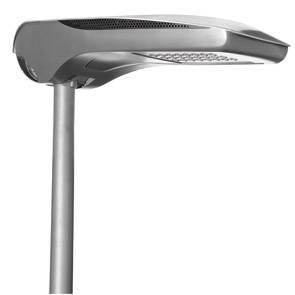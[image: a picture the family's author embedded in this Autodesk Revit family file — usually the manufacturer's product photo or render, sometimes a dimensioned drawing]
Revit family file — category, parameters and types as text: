
# Revit family: Lighting-StreetLighting-GEWISS-STREET[O3]-LED_OPTIC_ST1
name_source: partatom
category: Apparecchi per illuminazione
units: mm (PartAtom-declared; Revit-internal decimal feet)

## family parameters
Basato su piano di lavoro = No
Condiviso = No
Numero OmniClass = 23.80.70.14.21
Punto di calcolo locali = No
Quota connettore circolare = Usa diametro
Sempre verticale = Sì
Sorgente d'illuminazione = No
Taglio con vuoti quando caricato = No
Tipo di parte = Normale
Titolo OmniClass = Street and Roadway Lighting

## types (15) — shared parameters
Altezza da terra testa staffa = 822 mm
Application = External
Carico apparente = 68 VA
Catalogue = LIGHTING
Catalogue Range = STREET [O3]
Colour = Graphite/Aluminium
Commenti sul wattaggio = 68W
IDF = e1037118-10e4-4194-a64e-daf49fc1f628
IDT = a85e433dc89b4111a164f9b8ba35bb1e
IP degree = IP66
Immagine tipo = GW87502.jpg
Insulation class = II
LED Life time (L80B10) = 100000H
LED Life time (L90B20) = 50000H
L_staffa = 120 mm  [stored 0.393701 ft]
Lamp = LED
Lampada = LED
Maximum surface exposed to the wind = 0,26M2
Minimum distance from the illuminated object = 1M
Numero di poli = 2
Optic = ST1 - ULOR: 0%
Photobiologic Risk = RG1/RG2 @ 20cm
Produttore = GEWISS S.p.A.
SEO = Street lighting
Shock resistance = IK08 BODY - IK06 LENS
Struttura = <Per categoria>
Technical sheet = https://www.gewiss.com
Tilt adjustable = ±20° bracket - 0°÷20° pole head
URL = https://www.gewiss.com
Version file RFA = 20.11
Vetro = GEWISS - Led - lm 650 / Temp_3000_K
Voltage: = 220/240 V - 50/60 Hz
Voltaggio = 230 V
Warranty = 5 years

## per-type parameters (varying)
| type | Colour temperature | Colour temperature: | Descrizione | Driver type | EAN code | Electrocod | LED LifeTime (L80B20) | LED current | Lumen output (lm) | Material | Modello | No. Chorus modules | Nominal flux (lm) | Number of modules | Operating temperature: | Power supply operation | Risk photobiological | System power | Typology | Voltage | Weight (kg) | Weight (kg): | Working temperature |
| GW87413 - STREET LED 4M 4000K 700mA STR. | 4000 K (CRI 70) | 4000 K (CRI 70) | STREET LED 4M 4000K 700mA STR. | Constant Current Driver Led | 8011564830615 | 244C | 50000H | 700 mA | 12900 | Die-cast  aluminium | GW87413 | 4 (4x16 LED) | 15370 | 4 (4x16 LED) | -25 +35 °C |  | RG1/RG2 @ 20cm | 131W | Stand alone | 220/240 V - 50/60 Hz - Stand alone and/or possibility of dimmer 1-10 V | 10,3 | 10,3 | -25 +25 °C |
| GW87531 - STREET LED BIREG.2M 4000K 550mA STR | 4000 K (CRI 70) | 4000 K (CRI 70) | STREET LED BI-PO. 2M 4000K 530mA STREET | Constant Current Driver Led | 8011564782914 | 244C | 50000H | 530mA | 5890 | Die-cast  aluminium | GW87531 | 2 (2x16 LED) | 7020 | 2 (2x16 LED) | -25 +50 °C | Bi power | RG1/RG2 @ 20cm | 54W |  | 220/240 V - 50/60 Hz - Bi-power with self-learning | 9,1 | 9,1 | -25 +25 °C |
| GW87412V - STREET LED 3M 4000K 700mA STREET |  | 4000 K (CRI>70) | STREET LED 3M 4000K 700mA STR |  |  | 244C |  | 700 mA | 9860 |  | GW87412V |  | 11740 | 3 (3x16 LED) | -25 +25 °C |  |  | 99W | Programmable (5 step) | 220/240 V - 50/60 Hz - Stand alone e/o Programmabile 5 Step |  | 9,59999999999999 |  |
| GW87534 - STREET LED BIREG.5M 4000K 550mA STR | 4000 K (CRI 70) | 4000 K (CRI 70) | STREET LED BI-PO. 5M 4000K 530mA STREET | Constant Current Driver Led | 8011564782945 | 244B | 50000H | 530mA | 13870 | Die-cast  aluminium | GW87534 | 5 (5x16 LED) | 16530 | 5 (5x16 LED) | -25 +40 °C | Bi power | RG1/RG2 @ 20cm | 129W |  | 220/240 V - 50/60 Hz - Bi-power with self-learning | 10,9 | 10,9 | -25 +25 °C |
| GW87413V - STREET LED 4M 4000K 700mA STR. |  | 4000 K (CRI>70) | STREET LED 4M 4000K 700mA STR |  |  | 244C |  | 700 mA | 12900 |  | GW87413V |  | 15370 | 4 (4x16 LED) | -25 +25 °C |  |  | 131W | Programmable (5 step) | 220/240 V - 50/60 Hz - Stand alone e/o Programmabile 5 Step |  | 10,3 |  |
| GW87410 - STREET LED 1M 4000K 700mA STREET | 4000 K (CRI 70) | 4000 K (CRI 70) | STREET LED 1M 4000K 700mA STREET | Constant Current Driver Led | 8011564804654 | 244C | 50000H | 700 mA | 3470 | Die-cast  aluminium | GW87410 | 1 (1x16 LED) | 4140 | 1 (1x16 LED) | -25 +50 °C |  | RG1/RG2 @ 20cm | 37W | Stand alone | 220/240 V - 50/60 Hz - Stand alone and/or possibility of dimmer 1-10 V | 8,5 | 8,5 | -25 +25 °C |
| GW87414 - STREET ST1 5M 4000K 550mA 220/240 | 4000 K (CRI 70) | 4000 K (CRI 70) | STREET ST1 5M 4000K 550mA 220/240 | Constant Current Driver Led | 8011564863125 | 244C | 50000H | 550 mA | 13740 | Die-cast  aluminium | GW87414 | 5 (5x16 LED) | 16360 | 5 (5x16 LED) | -25 +40 °C |  | RG1/RG2 @ 20cm | 127W | Stand alone | 220/240 V - 50/60 Hz - Stand alone and/or possibility of dimmer 1-10 V | 10,9 | 10,9 | -25 +25 °C |
| GW87414V - STREET ST1 5M 4000K 550mA 220/240 |  | 4000 K (CRI>70) | STREET ST1 5M 4000K 550mA 220/240 |  |  | 244C |  | 550 mA | 13740 |  | GW87414V |  | 16360 | 5 (5x16 LED) | -25 +25 °C |  |  | 127W | Programmable (5 step) | 220/240 V - 50/60 Hz - Stand alone e/o Programmabile 5 Step |  | 10,9 |  |
| GW87410V - STREET LED 1M 4000K 700mA STREET |  | 4000 K (CRI>70) | STREET LED 1M 4000K 700mA STR |  |  | 244C |  | 700 mA | 3470 |  | GW87410V |  | 4140 | 1 (1x16 LED) | -25 +25 °C |  |  | 37W | Programmable (5 step) | 220/240 V - 50/60 Hz - Stand alone e/o Programmabile 5 Step |  | 8,5 |  |
| GW87412 - STREET LED 3M 4000K 700mA STREET | 4000 K (CRI 70) | 4000 K (CRI 70) | STREET LED 3M 4000K 700mA STREET | Constant Current Driver Led | 8011564804630 | 244C | 50000H | 700 mA | 9860 | Die-cast  aluminium | GW87412 | 3 (3x16 LED) | 11740 | 3 (3x16 LED) | -25 +40 °C |  | RG1/RG2 @ 20cm | 99W | Stand alone | 220/240 V - 50/60 Hz - Stand alone and/or possibility of dimmer 1-10 V | 9,6 | 9,6 | -25 +25 °C |
| GW87411V - STREET LED 2M 4000K 700mA STREET |  | 4000 K (CRI>70) | STREET LED 2M 4000K 700mA STR |  |  | 244C |  | 700 mA | 6760 |  | GW87411V |  | 8050 | 2 (2x16 LED) | -25 +25 °C |  |  | 68W | Programmable (5 step) | 220/240 V - 50/60 Hz - Stand alone e/o Programmabile 5 Step |  | 9,09999999999999 |  |
| GW87530 - STREET LED BIREG.1M 4000K 550mA STR | 4000 K (CRI 70) | 4000 K (CRI 70) | STREET LED BI-PO. 1M 4000K 530mA STREET | Constant Current Driver Led | 8011564804661 | 244C | 50000H | 530mA | 3030 | Die-cast  aluminium | GW87530 | 1 (1x16 LED) | 3610 | 1 (1x16 LED) | -25 +50 °C | Bi power | RG1/RG2 @ 20cm | 31W |  | 220/240 V - 50/60 Hz - Bi-power with self-learning | 8,5 | 8,5 | -25 +25 °C |
| GW87533 - STREET LED BIREG.4M 4000K 550mA STR | 4000 K (CRI 70) | 4000 K (CRI 70) | STREET LED BI-PO. 4M 4000K 530mA STREET | Constant Current Driver Led | 8011564782938 | 244C | 50000H | 530mA | 11240 | Die-cast  aluminium | GW87533 | 4 (4x16 LED) | 13400 | 4 (4x16 LED) | -25 +50 °C | Bi power | RG1/RG2 @ 20cm | 105W |  | 220/240 V - 50/60 Hz - Bi-power with self-learning | 10,3 | 10,3 | -25 +25 °C |
| GW87411 - STREET LED 2M 4000K 700mA STREET | 4000 K (CRI 70) | 4000 K (CRI 70) | STREET LED 2M 4000K 700mA STREET | Constant Current Driver Led | 8011564804647 | 244C | 50000H | 700 mA | 6760 | Die-cast  aluminium | GW87411 | 2 (2x16 LED) | 8050 | 2 (2x16 LED) | -25 +35 °C |  | RG1/RG2 @ 20cm | 68W | Stand alone | 220/240 V - 50/60 Hz - Stand alone and/or possibility of dimmer 1-10 V | 9,1 | 9,1 | -25 +25 °C |
| GW87532 - STREET LED BIREG.3M 4000K 550mA STR | 4000 K (CRI 70) | 4000 K (CRI 70) | STREET LED BI-PO. 3M 4000K 530mA STREET | Constant Current Driver Led | 8011564782921 | 244C | 50000H | 530mA | 8590 | Die-cast  aluminium | GW87532 | 3 (3x16 LED) | 10230 | 3 (3x16 LED) | -25 +50 °C | Bi power | RG1/RG2 @ 20cm | 81W |  | 220/240 V - 50/60 Hz - Bi-power with self-learning | 9,7 | 9,7 | -25 +25 °C |

note: [stored X ft] marks values corroborated as IEEE doubles in the binary element streams (Revit-internal decimal feet)
